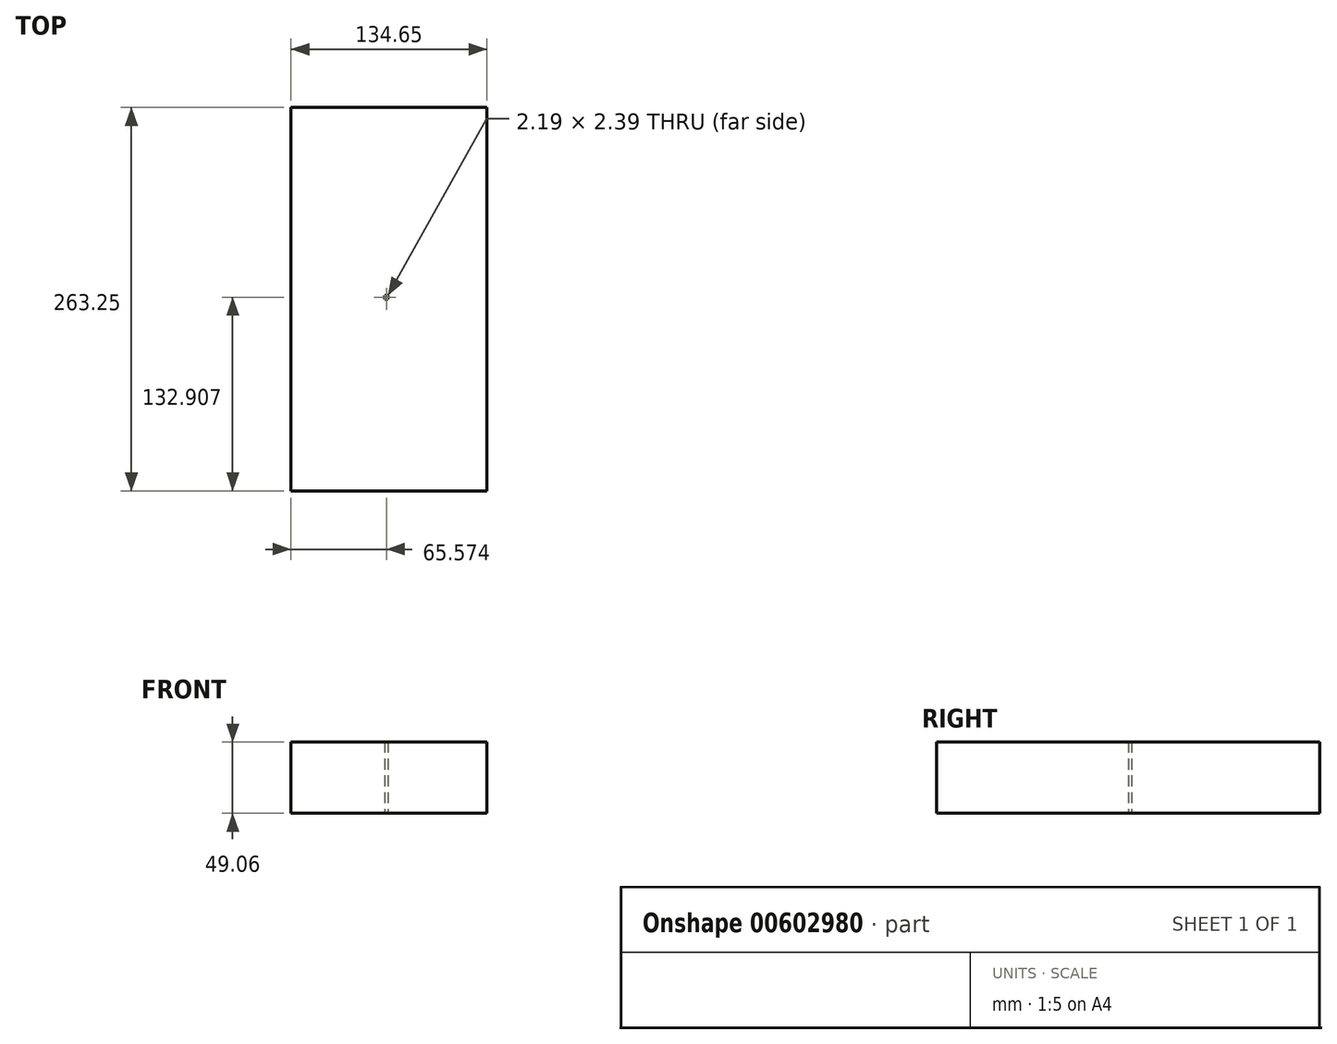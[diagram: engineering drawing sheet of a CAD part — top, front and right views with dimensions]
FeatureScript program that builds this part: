
annotation { "Feature Type Name" : "Feature", "Feature Type Description" : "" }
export const myFeature = defineFeature(function(context is Context, id is Id, definition is map)
    precondition{}
    {
        {
            var Q0;
            Q0=qCreatedBy(makeId("Top.planeOp"),FACE);
            var sketch = newSketch(context, id + "F0", { "sketchPlane" : qUnion([Q0])});
            skLineSegment(sketch, "E0.bottom", {"start": v(0, 0) * mm, "end": v(0, 0) * mm});
            skLineSegment(sketch, "E0.top", {"start": v(0, 0) * mm, "end": v(0, 0) * mm});
            skLineSegment(sketch, "E0.left", {"start": v(0, 0) * mm, "end": v(0, 0) * mm});
            skLineSegment(sketch, "E0.right", {"start": v(0, 0) * mm, "end": v(0, 0) * mm});
            skPoint(sketch, "E0.middle", {"position": v(0, 0) * mm});
            skLineSegment(sketch, "E1.bottom", {"start": v(0, 0) * mm, "end": v(-2.2, 0) * mm});
            skLineSegment(sketch, "E1.top", {"start": v(0, 2.4) * mm, "end": v(-2.2, 2.4) * mm});
            skLineSegment(sketch, "E1.left", {"start": v(0, 0) * mm, "end": v(0, 2.4) * mm});
            skLineSegment(sketch, "E1.right", {"start": v(-2.2, 0) * mm, "end": v(-2.2, 2.4) * mm});
            skPoint(sketch, "E1.middle", {"position": v(-1.1, 1.2) * mm});
            skLineSegment(sketch, "E2.bottom", {"start": v(67.98, -131.71) * mm, "end": v(-66.67, -131.71) * mm});
            skLineSegment(sketch, "E2.top", {"start": v(67.98, 131.54) * mm, "end": v(-66.67, 131.54) * mm});
            skLineSegment(sketch, "E2.left", {"start": v(67.98, -131.71) * mm, "end": v(67.98, 131.54) * mm});
            skLineSegment(sketch, "E2.right", {"start": v(-66.67, -131.71) * mm, "end": v(-66.67, 131.54) * mm});
            skPoint(sketch, "E2.middle", {"position": v(0.65, -0.08) * mm});
            skSolve(sketch);
        }
        {
            var Q0;
            Q0=makeQuery(id+"F0.imprint","IMPRINT",FACE,{"disambiguationData":[TD([[makeQuery(id+"F0.imprint","IMPRINT",EDGE,{"derivedFrom":sQuery(id+"F0.wireOp",EDGE,"E1.bottom")}),1.0]])]});
            extrude(context, id + "F1", {"entities" : qUnion([Q0]), "depth" : 49.06 * mm, "offsetDistance" : 25.4 * mm});
        }
    });
